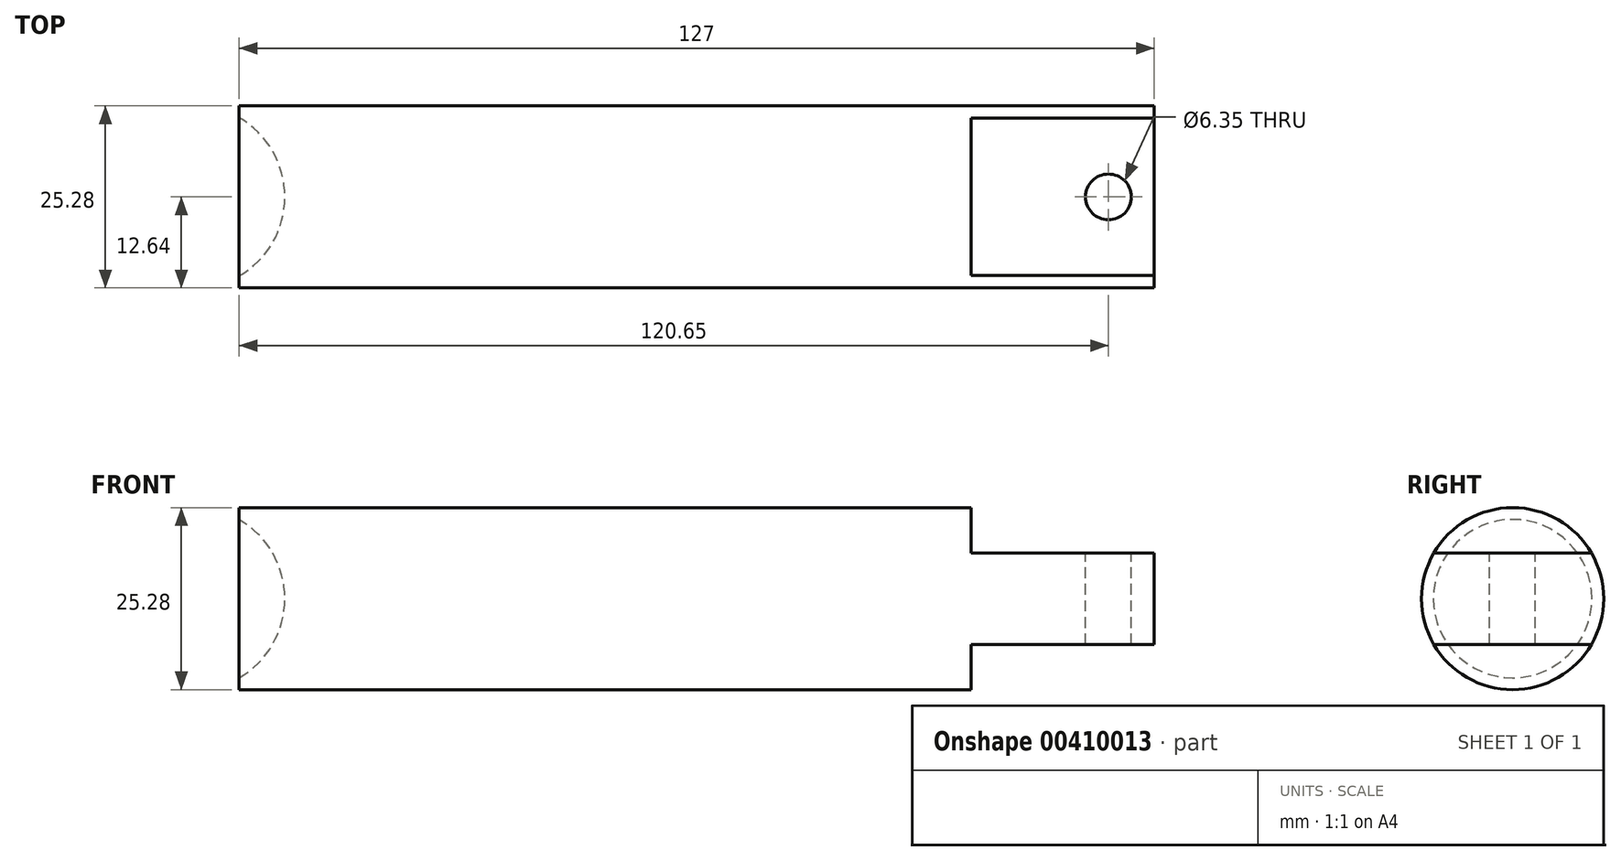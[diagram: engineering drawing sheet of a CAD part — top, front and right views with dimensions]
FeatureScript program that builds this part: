
annotation { "Feature Type Name" : "Feature", "Feature Type Description" : "" }
export const myFeature = defineFeature(function(context is Context, id is Id, definition is map)
    precondition{}
    {
        {
            var Q0;
            Q0=qCreatedBy(makeId("Right.planeOp"),FACE);
            var sketch = newSketch(context, id + "F0", { "sketchPlane" : qUnion([Q0])});
            skCircle(sketch, "E0", {"center": v(0, 0) * mm, "radius": 12.64 * mm});
            skSolve(sketch);
        }
        {
            var Q0;
            Q0 = qSketchRegion(id + "F0", true);
            extrude(context, id + "F1", {"entities" : qUnion([Q0]), "depth" : 127 * mm});
        }
        {
            var Q0;
            Q0=qCreatedBy(makeId("Front.planeOp"),FACE);
            var sketch = newSketch(context, id + "F2", { "sketchPlane" : qUnion([Q0])});
            skLineSegment(sketch, "E1.bottom", {"start": v(101.6, 33.96) * mm, "end": v(127, 33.96) * mm});
            skLineSegment(sketch, "E1.top", {"start": v(101.6, 6.35) * mm, "end": v(127, 6.35) * mm});
            skLineSegment(sketch, "E1.left", {"start": v(101.6, 33.96) * mm, "end": v(101.6, 6.35) * mm});
            skLineSegment(sketch, "E1.right", {"start": v(127, 33.96) * mm, "end": v(127, 6.35) * mm});
            skLineSegment(sketch, "E2", {"start": v(-31.63, 0) * mm, "end": v(172.8, 0) * mm, "construction": true});
            skLineSegment(sketch, "E3.MirrorCS", {"start": v(101.6, -6.35) * mm, "end": v(127, -6.35) * mm});
            skLineSegment(sketch, "E4.MirrorCS", {"start": v(101.6, -33.96) * mm, "end": v(101.6, -6.35) * mm});
            skLineSegment(sketch, "E5.MirrorCS", {"start": v(127, -33.96) * mm, "end": v(127, -6.35) * mm});
            skLineSegment(sketch, "E6.MirrorCS", {"start": v(101.6, -33.96) * mm, "end": v(127, -33.96) * mm});
            skSolve(sketch);
        }
        {
            var Q0;
            Q0 = qSketchRegion(id + "F2", true);
            extrude(context, id + "F3", {"entities" : qUnion([Q0]), "operationType" : NewBodyOperationType.REMOVE, "endBound" : BoundingType.SYMMETRIC, "oppositeDirection" : true, "depth" : 25.4 * mm});
        }
        {
            var Q0;
            Q0=makeQuery(id+"F3.boolean.opBoolean","COPY",FACE,{"derivedFrom":makeQuery(id+"F3.opExtrude","SWEPT_FACE",FACE,{"disambiguationData":[OSD([sQuery(id+"F2.wireOp",EDGE,"E1.top")])]})});
            var sketch = newSketch(context, id + "F4", { "sketchPlane" : qUnion([Q0])});
            skLineSegment(sketch, "E7", {"start": v(-37.5, 0) * mm, "end": v(133.03, 0) * mm, "construction": true});
            skLineSegment(sketch, "E8", {"start": v(120.65, 18.74) * mm, "end": v(120.65, -26.78) * mm, "construction": true});
            skCircle(sketch, "E9", {"center": v(120.65, 0) * mm, "radius": 3.18 * mm});
            skSolve(sketch);
        }
        {
            var Q0;
            Q0 = qSketchRegion(id + "F4", true);
            extrude(context, id + "F5", {"entities" : qUnion([Q0]), "operationType" : NewBodyOperationType.REMOVE, "endBound" : BoundingType.THROUGH_ALL, "oppositeDirection" : true, "depth" : 25.4 * mm});
        }
        {
            var Q0;
            Q0=qCreatedBy(makeId("Top.planeOp"),FACE);
            var sketch = newSketch(context, id + "F6", { "sketchPlane" : qUnion([Q0])});
            skLineSegment(sketch, "E10", {"start": v(-6.35, 14.12) * mm, "end": v(-6.35, -20.83) * mm, "construction": true});
            skLineSegment(sketch, "E11", {"start": v(-30.48, 0) * mm, "end": v(37.4, 0) * mm, "construction": true});
            skArc(sketch, "E12", {"start": v(-6.35, -12.7) * mm, "mid": v(6.35, 0) * mm, "end": v(-6.35, 12.7) * mm});
            skLineSegment(sketch, "E13", {"start": v(-6.35, 12.7) * mm, "end": v(-6.35, -12.7) * mm});
            skSolve(sketch);
        }
        {
            var Q0;
            Q0 = qSketchRegion(id + "F6", true);
            var Q1;
            Q1=sQuery(id+"F6.wireOp",EDGE,"E10");
            revolve(context, id + "F7", {"operationType" : NewBodyOperationType.REMOVE, "entities" : qUnion([Q0]), "axis" : qUnion([Q1]), "revolveType" : RevolveType.FULL, "oppositeDirection" : true});
        }
    });
